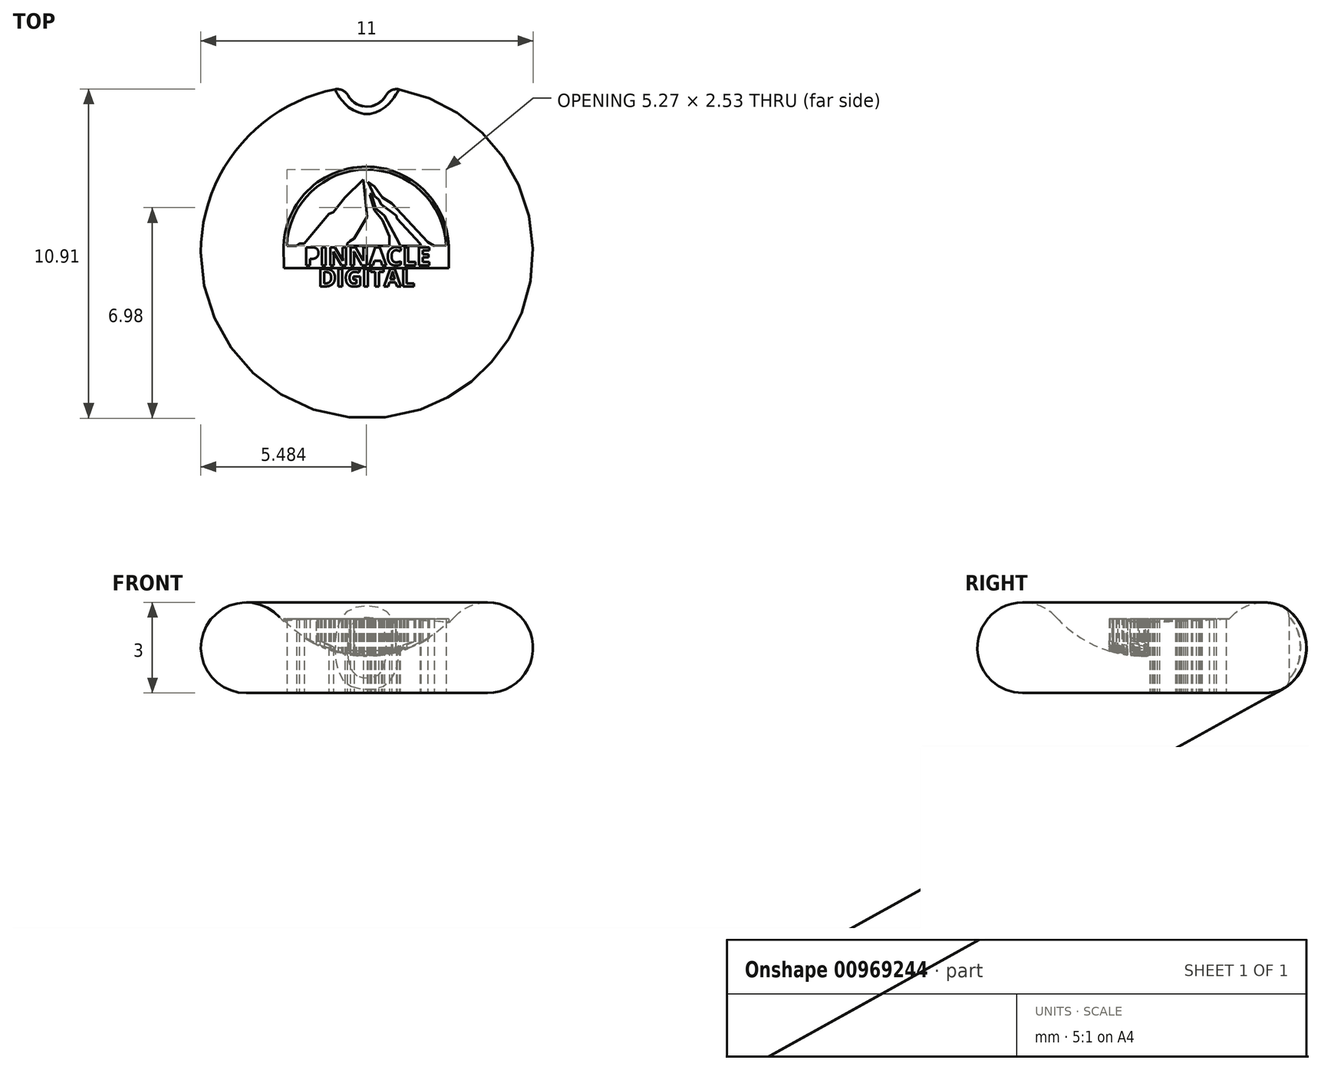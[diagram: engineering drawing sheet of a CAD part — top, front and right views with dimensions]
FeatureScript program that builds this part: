
annotation { "Feature Type Name" : "Feature", "Feature Type Description" : "" }
export const myFeature = defineFeature(function(context is Context, id is Id, definition is map)
    precondition{}
    {
        {
            var Q0;
            Q0=qCreatedBy(makeId("Front.planeOp"),FACE);
            var sketch = newSketch(context, id + "F0", { "sketchPlane" : qUnion([Q0])});
            skCircle(sketch, "E0", {"center": v(-4, 1.5) * mm, "radius": 1.5 * mm});
            skArc(sketch, "E1", {"start": v(-2.89, 2.5) * mm, "mid": v(-1.58, 1.56) * mm, "end": v(0, 1.23) * mm});
            skLineSegment(sketch, "E2", {"start": v(-4.23, 0) * mm, "end": v(0, 0) * mm});
            skLineSegment(sketch, "E3", {"start": v(0, 0) * mm, "end": v(0, 1.23) * mm});
            skSolve(sketch);
        }
        {
            var Q0;
            Q0=qSketchRegion(id+"F0",true);
            var Q1;
            Q1=sQuery(id+"F0.wireOp",EDGE,"E3");
            revolve(context, id + "F1", {"surfaceOperationType" : NewSurfaceOperationType.NEW, "entities" : qUnion([Q0]), "axis" : qUnion([Q1]), "revolveType" : RevolveType.FULL});
        }
        {
            var Q0;
            Q0=qCreatedBy(makeId("Top.planeOp"),FACE);
            var sketch = newSketch(context, id + "F2", { "sketchPlane" : qUnion([Q0])});
            skCircle(sketch, "E4", {"center": v(0, 5.54) * mm, "radius": 0.72 * mm});
            skSolve(sketch);
        }
        {
            var Q0;
            Q0=qSketchRegion(id+"F2",true);
            extrude(context, id + "F3", {"entities" : qUnion([Q0]), "operationType" : NewBodyOperationType.REMOVE, "depth" : 25 * mm, "offsetDistance" : 25 * mm});
        }
        {
            var Q0;
            Q0=makeQuery(id+"F3.boolean.opBoolean","INTERSECT",EDGE,{"derivedFrom":[makeQuery(id+"F1.opRevolve","SWEPT_FACE",FACE,{"disambiguationData":[OSD([sQuery(id+"F0.wireOp",EDGE,"E0")])]}),makeQuery(id+"F3.opExtrude","SWEPT_FACE",FACE,{"disambiguationData":[OSD([sQuery(id+"F2.wireOp",EDGE,"E4")])]})]});
            fillet(context, id + "F4", {"entities" : qUnion([Q0]), "radius" : .4 * mm, "tangentPropagation" : true, "allowEdgeOverflow" : false});
        }
        {
            var Q0;
            Q0=qCreatedBy(makeId("Top.planeOp"),FACE);
            var sketch = newSketch(context, id + "F5", { "sketchPlane" : qUnion([Q0])});
            skArc(sketch, "E5", {"start": v(2.71, 0.22) * mm, "mid": v(-0.03, 2.84) * mm, "end": v(-2.76, 0.22) * mm});
            skArc(sketch, "E6", {"start": v(2.62, 0.23) * mm, "mid": v(-0.02, 2.74) * mm, "end": v(-2.65, 0.22) * mm});
            skLineSegment(sketch, "E7", {"start": v(-2.65, 0.22) * mm, "end": v(-2.33, 0.22) * mm});
            skLineSegment(sketch, "E8", {"start": v(-2.33, 0.22) * mm, "end": v(-2.25, 0.3) * mm});
            skLineSegment(sketch, "E9", {"start": v(-2.25, 0.3) * mm, "end": v(-2.08, 0.3) * mm});
            skLineSegment(sketch, "E10", {"start": v(-2.08, 0.3) * mm, "end": v(-1.27, 1.26) * mm});
            skLineSegment(sketch, "E11", {"start": v(-1.27, 1.26) * mm, "end": v(-1.12, 1.33) * mm});
            skLineSegment(sketch, "E12", {"start": v(-1.12, 1.33) * mm, "end": v(-0.73, 1.82) * mm});
            skLineSegment(sketch, "E13", {"start": v(-0.73, 1.82) * mm, "end": v(-0.12, 2.41) * mm});
            skLineSegment(sketch, "E14", {"start": v(-0.12, 2.41) * mm, "end": v(0, 1.17) * mm});
            skLineSegment(sketch, "E15", {"start": v(0, 1.17) * mm, "end": v(-0.43, 0.45) * mm});
            skLineSegment(sketch, "E16", {"start": v(-0.43, 0.45) * mm, "end": v(-0.55, 0.38) * mm});
            skLineSegment(sketch, "E17", {"start": v(-0.55, 0.38) * mm, "end": v(-0.65, 0.3) * mm});
            skLineSegment(sketch, "E18", {"start": v(-0.65, 0.3) * mm, "end": v(-0.65, 0.22) * mm});
            skLineSegment(sketch, "E19", {"start": v(-0.65, 0.22) * mm, "end": v(0.75, 0.22) * mm});
            skLineSegment(sketch, "E20", {"start": v(0.75, 0.22) * mm, "end": v(0.75, 0.53) * mm});
            skLineSegment(sketch, "E21", {"start": v(0.75, 0.53) * mm, "end": v(0.51, 1.06) * mm});
            skLineSegment(sketch, "E22", {"start": v(0.51, 1.06) * mm, "end": v(0.25, 1.4) * mm});
            skLineSegment(sketch, "E23", {"start": v(0.25, 1.4) * mm, "end": v(0.1, 1.92) * mm});
            skLineSegment(sketch, "E24", {"start": v(0.1, 1.92) * mm, "end": v(0.14, 1.93) * mm});
            skLineSegment(sketch, "E25", {"start": v(0.14, 1.93) * mm, "end": v(0.29, 1.46) * mm});
            skLineSegment(sketch, "E26", {"start": v(0.29, 1.46) * mm, "end": v(0.58, 1.22) * mm});
            skLineSegment(sketch, "E27", {"start": v(0.58, 1.22) * mm, "end": v(1.08, 0.3) * mm});
            skLineSegment(sketch, "E28", {"start": v(1.08, 0.3) * mm, "end": v(1.1, 0.22) * mm});
            skLineSegment(sketch, "E29", {"start": v(1.1, 0.22) * mm, "end": v(1.79, 0.22) * mm});
            skLineSegment(sketch, "E30", {"start": v(1.79, 0.22) * mm, "end": v(1.76, 0.3) * mm});
            skLineSegment(sketch, "E31", {"start": v(1.76, 0.3) * mm, "end": v(1, 1.11) * mm});
            skLineSegment(sketch, "E32", {"start": v(1, 1.11) * mm, "end": v(0.97, 1.22) * mm});
            skLineSegment(sketch, "E33", {"start": v(0.97, 1.22) * mm, "end": v(0.47, 1.59) * mm});
            skLineSegment(sketch, "E34", {"start": v(0.47, 1.59) * mm, "end": v(0.39, 1.74) * mm});
            skLineSegment(sketch, "E35", {"start": v(0.39, 1.74) * mm, "end": v(0.25, 1.87) * mm});
            skLineSegment(sketch, "E36", {"start": v(0.25, 1.87) * mm, "end": v(0.04, 2.33) * mm});
            skLineSegment(sketch, "E37", {"start": v(0.04, 2.33) * mm, "end": v(0.25, 2.17) * mm});
            skLineSegment(sketch, "E38", {"start": v(0.25, 2.17) * mm, "end": v(0.51, 1.82) * mm});
            skLineSegment(sketch, "E39", {"start": v(0.51, 1.82) * mm, "end": v(0.82, 1.63) * mm});
            skLineSegment(sketch, "E40", {"start": v(0.82, 1.63) * mm, "end": v(2.01, 0.34) * mm});
            skLineSegment(sketch, "E41", {"start": v(2.01, 0.34) * mm, "end": v(2.23, 0.22) * mm});
            skLineSegment(sketch, "E42", {"start": v(2.23, 0.22) * mm, "end": v(2.62, 0.23) * mm});
            skLineSegment(sketch, "E43", {"start": v(-2.76, 0.22) * mm, "end": v(-2.74, -0.52) * mm});
            skLineSegment(sketch, "E44", {"start": v(-2.74, -0.52) * mm, "end": v(2.72, -0.52) * mm});
            skLineSegment(sketch, "E45", {"start": v(2.72, -0.52) * mm, "end": v(2.71, 0.22) * mm});
            skText(sketch, "E46", { "text": "PINNACLE", "fontName": "OpenSans-Bold.ttf"});
            skText(sketch, "E47", { "text": "DIGITAL", "fontName": "OpenSans-Bold.ttf"});
            const initialGuessF5  = {"E46": [-0.00209, -0.00043, 1, 0, 0.0006], "E47": [-0.00161, -0.00113, 1, 0, 0.00058]};
            skSetInitialGuess(sketch, initialGuessF5);
            skSolve(sketch);
        }
        {
            var Q0;
            Q0 = qSketchRegion(id + "F5", true);
            extrude(context, id + "F6", {"entities" : qUnion([Q0]), "operationType" : NewBodyOperationType.ADD, "depth" : 2.45 * mm, "offsetDistance" : 25 * mm});
        }
        {
            var Q0;
            Q0=makeQuery(id+"F5.imprint","IMPRINT",FACE,{"disambiguationData":[TD([[makeQuery(id+"F5.imprint","IMPRINT",EDGE,{"derivedFrom":sQuery(id+"F5.wireOp",EDGE,"E6")}),1.0]])]});
            var Q1;
            Q1 = qConstructionFilter(qBodyType(qCreatedBy(id + "F5" ,EDGE), BodyType.WIRE), ConstructionObject.NO);
            extrude(context, id + "F7", {"entities" : qUnion([Q0]), "operationType" : NewBodyOperationType.REMOVE, "surfaceEntities" : qUnion([Q1]), "endBound" : BoundingType.THROUGH_ALL, "depth" : 25 * mm, "offsetDistance" : 25 * mm});
        }
    });
